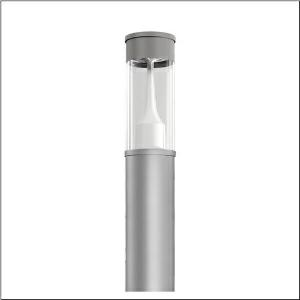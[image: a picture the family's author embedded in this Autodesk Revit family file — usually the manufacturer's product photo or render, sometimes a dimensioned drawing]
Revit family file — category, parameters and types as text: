
# Revit family: city-light_400_iq___p1_0a_5xa5305bf14hp_df67
name_source: partatom
category: Lighting Fixtures
units: mm (PartAtom-declared; Revit-internal decimal feet)

## family parameters
Cut with Voids When Loaded = No
Host = Face
Light Source = No
Part Type = Normal
Room Calculation Point = No
Round Connector Dimension = Use Diameter
Shared = No

## types (1)
- --- (1 x LED, 3890 lm, 33.6 W, 2200K)
    Apparent Load = 34 VA
    CIE Flux Codes = 31 62 91 95 100
    Color Rendering = 70
    Color Temperature = 2200K
    Default Elevation = 1800 mm
    Description = City-Light 400 iQ, light pillar, Module 540 iQ-SR, primary light control with 3 zone facetted reflector, of plastic, silver coated, highly specular, structured, primary optical cover: cover, of PMMA, transparent, partly coated, light distribution: P1.0a, primary light characteristic: strongly asymmetric, LED, High Power LED, rated luminous flux: 3.890lm, luminous efficacy: 116lm/W, light colour: 722, colour temperature: 2200K, control gear: iQ Street-Remote, control: pre-setting: logarithmic dimming characteristic, Street-Remote, Auto-Match, Temp-Guard, Lumen-Switch, Night-Set, Smart-Wire, Light-Fading, Desk-Remote (wireless, voltage-free reading and setting of iQ features in the workshop via application-optimized NFC function/RFID function), optimised constant luminous flux control (CLO 2.0), with terminal, 6-pole, max. 2.5mm², mains connection: 230..240V, AC, 50/60Hz, start of lifetime: 34W, end of service life: 36W, reduction: 15W, luminaire housing, cylindrical, of extruded aluminium section, coated, Siteco® metallic grey (DB 702S), length: 4.694mm, diameter: 200mm, Module 540 iQ-SR, traffic white (RAL 9016), equipment: Power, protection rating (complete): IP65, insulation class (complete): insulation class II (safety insulation), certification: CE, ENEC, VDE, packaging unit: 1 piece

Light Distribution: P1.0a
    Height = 500 mm
    Lamp = 1 x LED
    Lamp Light Flux = 3890 lm
    Lamp Power = 33.6 W
    Lamp count = 1
    Length = 200 mm  [stored 0.656168 ft]
    Luminous efficacy = 116 lm/W
    Manufacturer = Siteco
    ModVariant = No
    Model = 5XA5305BF14HP
    Mounting Place = Floor
    Mounting Type = Freestanding
    Number of Poles = 1
    OnlyDefault = Yes
    Power Factor = 1
    Product Name = City-Light 400 iQ | P1.0a
    Product group = light pillar
    ProductGroupID = 1301
    Protection Class = Protection class II
    Protection Degree = IP 65
    RLX_Detail_Level = 1
    RLX_Emergency_Light_Flux = 0 lm
    RLX_Emergency_Type = 0
    RLX_Emergency_Type_DB = No
    RlxData = <blob elided: 53473 chars, md5=a2a44735>
    Socket = socket
    Standby Power = 0 W
    System Light Flux = 3890 lm
    System Power = 34 W
    Type Comments = factory setting: luminous flux: 100 % | dim-lin: 254 | 695 mA
    Type Image = l_1006916.jpg
    URL = http://relux.com
    VarID = @adj_191805
    Voltage = 0 V
    Weight = 0.00 kg
    Width = 0 mm  [stored 0 ft]

note: [stored X ft] marks values corroborated as IEEE doubles in the binary element streams (Revit-internal decimal feet)

## geometry (parser evidence)
native form markers: Blend x4, Sweep x14
no freeform markers — native parametric forms only
